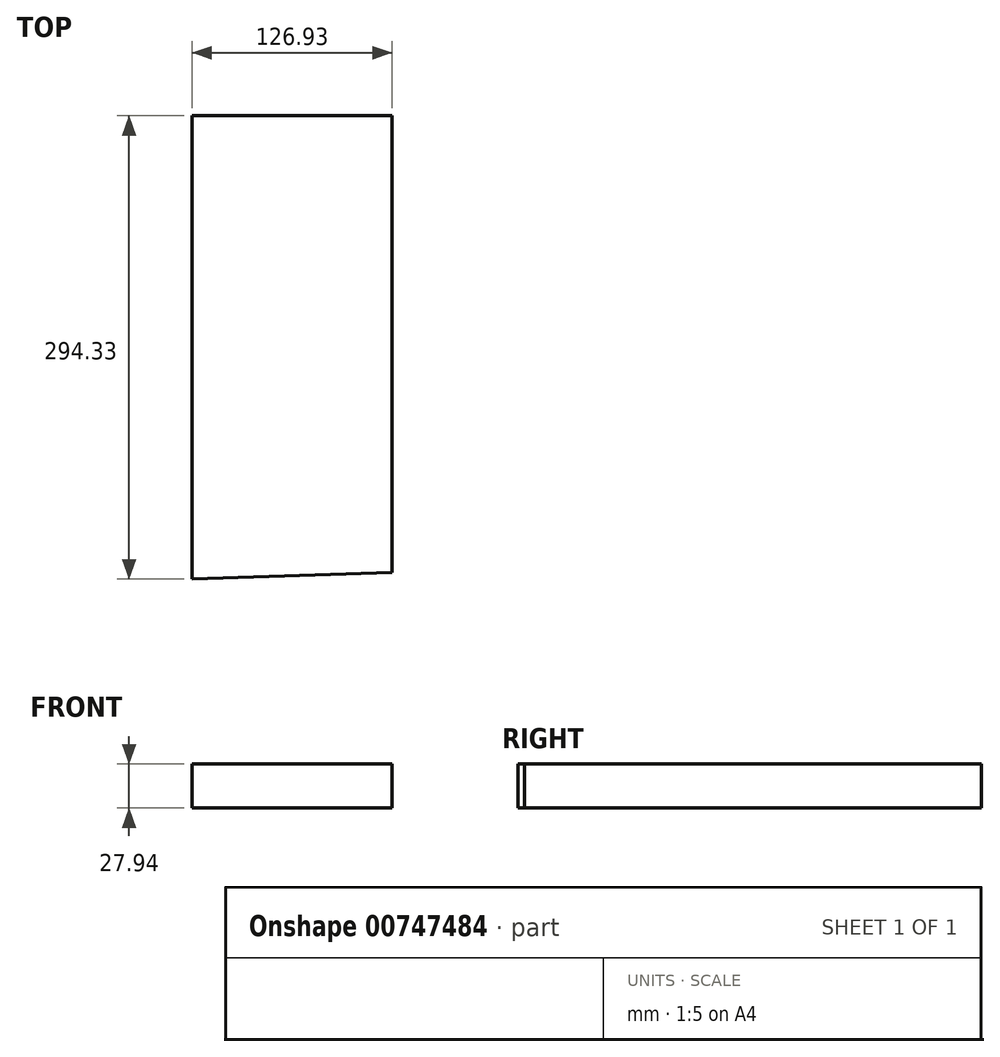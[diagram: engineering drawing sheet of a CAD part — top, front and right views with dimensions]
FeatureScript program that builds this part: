
annotation { "Feature Type Name" : "Feature", "Feature Type Description" : "" }
export const myFeature = defineFeature(function(context is Context, id is Id, definition is map)
    precondition{}
    {
        {
            var Q0;
            Q0=qCreatedBy(makeId("Top.planeOp"),FACE);
            var sketch = newSketch(context, id + "F0", { "sketchPlane" : qUnion([Q0])});
            skLineSegment(sketch, "E0", {"start": v(0, 0) * mm, "end": v(0, -294.33) * mm});
            skLineSegment(sketch, "E1", {"start": v(0, 0) * mm, "end": v(126.93, 0) * mm});
            skLineSegment(sketch, "E2", {"start": v(126.93, 0) * mm, "end": v(126.93, -290.07) * mm});
            skLineSegment(sketch, "E3", {"start": v(126.93, -290.07) * mm, "end": v(0, -294.33) * mm});
            skSolve(sketch);
        }
        {
            var Q0;
            Q0 = qSketchRegion(id + "F0", true);
            extrude(context, id + "F1", {"entities" : qUnion([Q0]), "depth" : 27.94 * mm, "offsetDistance" : 25.4 * mm});
        }
    });
